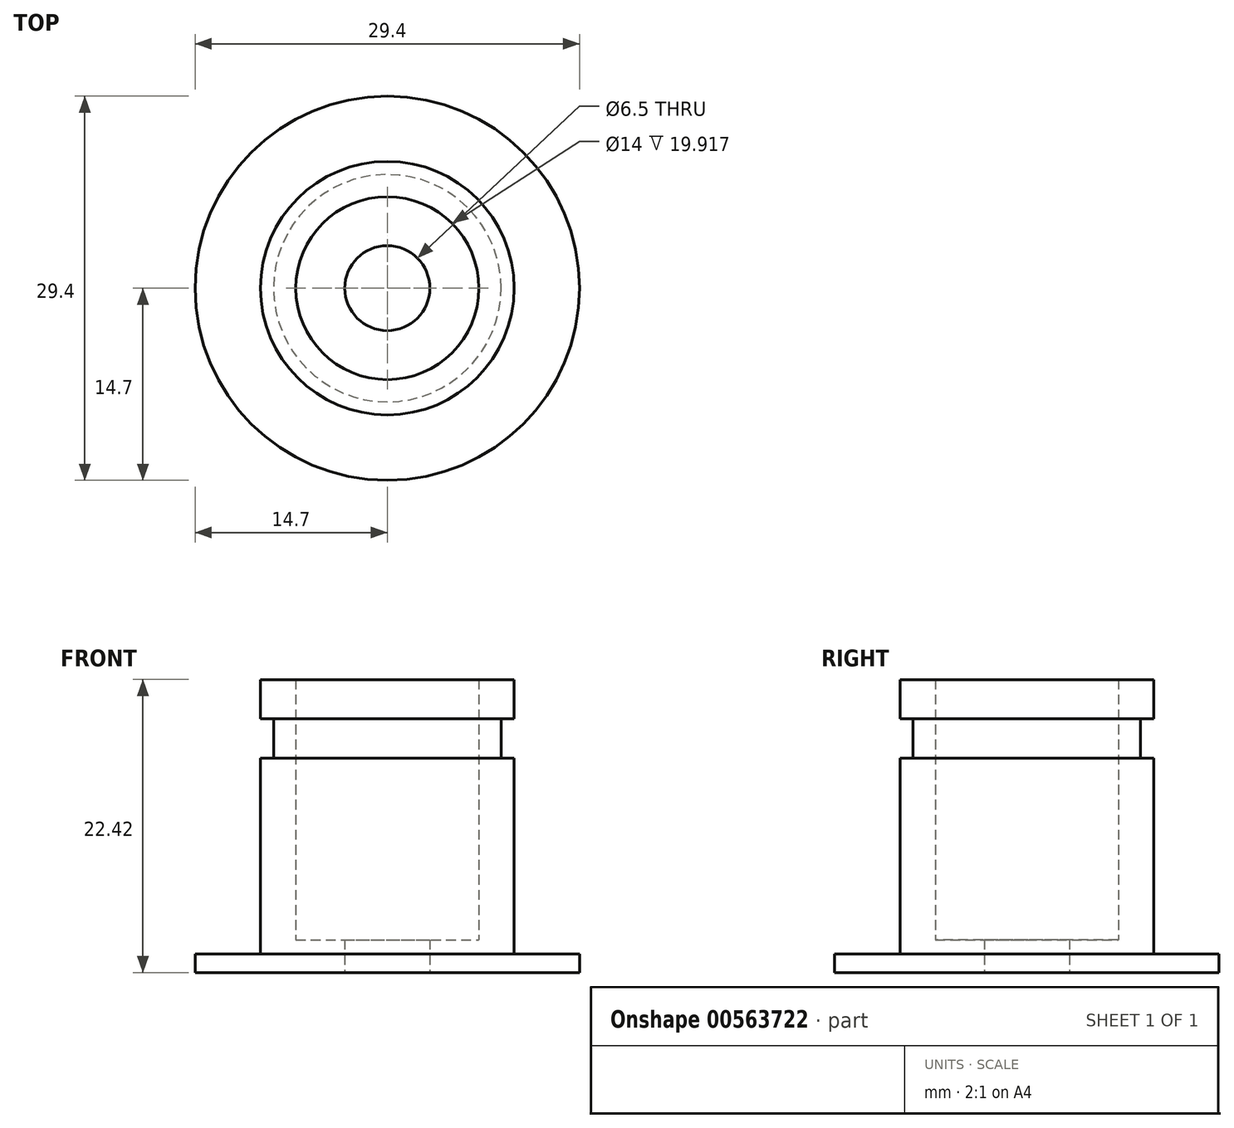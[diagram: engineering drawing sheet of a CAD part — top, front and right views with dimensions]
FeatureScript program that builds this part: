
annotation { "Feature Type Name" : "Feature", "Feature Type Description" : "" }
export const myFeature = defineFeature(function(context is Context, id is Id, definition is map)
    precondition{}
    {
        {
            var Q0;
            Q0=qCreatedBy(makeId("Front.planeOp"),FACE);
            var sketch = newSketch(context, id + "F0", { "sketchPlane" : qUnion([Q0])});
            skLineSegment(sketch, "E0", {"start": v(3.25, 0) * mm, "end": v(3.25, 2.5) * mm});
            skLineSegment(sketch, "E1", {"start": v(3.25, 2.5) * mm, "end": v(7, 2.5) * mm});
            skLineSegment(sketch, "E2", {"start": v(7, 2.5) * mm, "end": v(7, 22.42) * mm});
            skLineSegment(sketch, "E3", {"start": v(7, 22.42) * mm, "end": v(9.7, 22.42) * mm});
            skLineSegment(sketch, "E4", {"start": v(9.7, 22.42) * mm, "end": v(9.7, 19.42) * mm});
            skLineSegment(sketch, "E5", {"start": v(9.7, 19.42) * mm, "end": v(8.7, 19.42) * mm});
            skLineSegment(sketch, "E6", {"start": v(8.7, 19.42) * mm, "end": v(8.7, 16.42) * mm});
            skLineSegment(sketch, "E7", {"start": v(8.7, 16.42) * mm, "end": v(9.7, 16.42) * mm});
            skLineSegment(sketch, "E8", {"start": v(9.7, 16.42) * mm, "end": v(9.7, 1.42) * mm});
            skLineSegment(sketch, "E9", {"start": v(9.7, 1.42) * mm, "end": v(14.7, 1.42) * mm});
            skLineSegment(sketch, "E10", {"start": v(14.7, 1.42) * mm, "end": v(14.7, 0) * mm});
            skLineSegment(sketch, "E11", {"start": v(14.7, 0) * mm, "end": v(3.25, 0) * mm});
            skLineSegment(sketch, "E12", {"start": v(0, 0) * mm, "end": v(0, 16.74) * mm});
            skSolve(sketch);
        }
        {
            var Q0;
            Q0=qSketchRegion(id+"F0",true);
            var Q1;
            Q1=sQuery(id+"F0.wireOp",EDGE,"E12");
            revolve(context, id + "F1", {"entities" : qUnion([Q0]), "axis" : qUnion([Q1]), "revolveType" : RevolveType.FULL});
        }
    });
